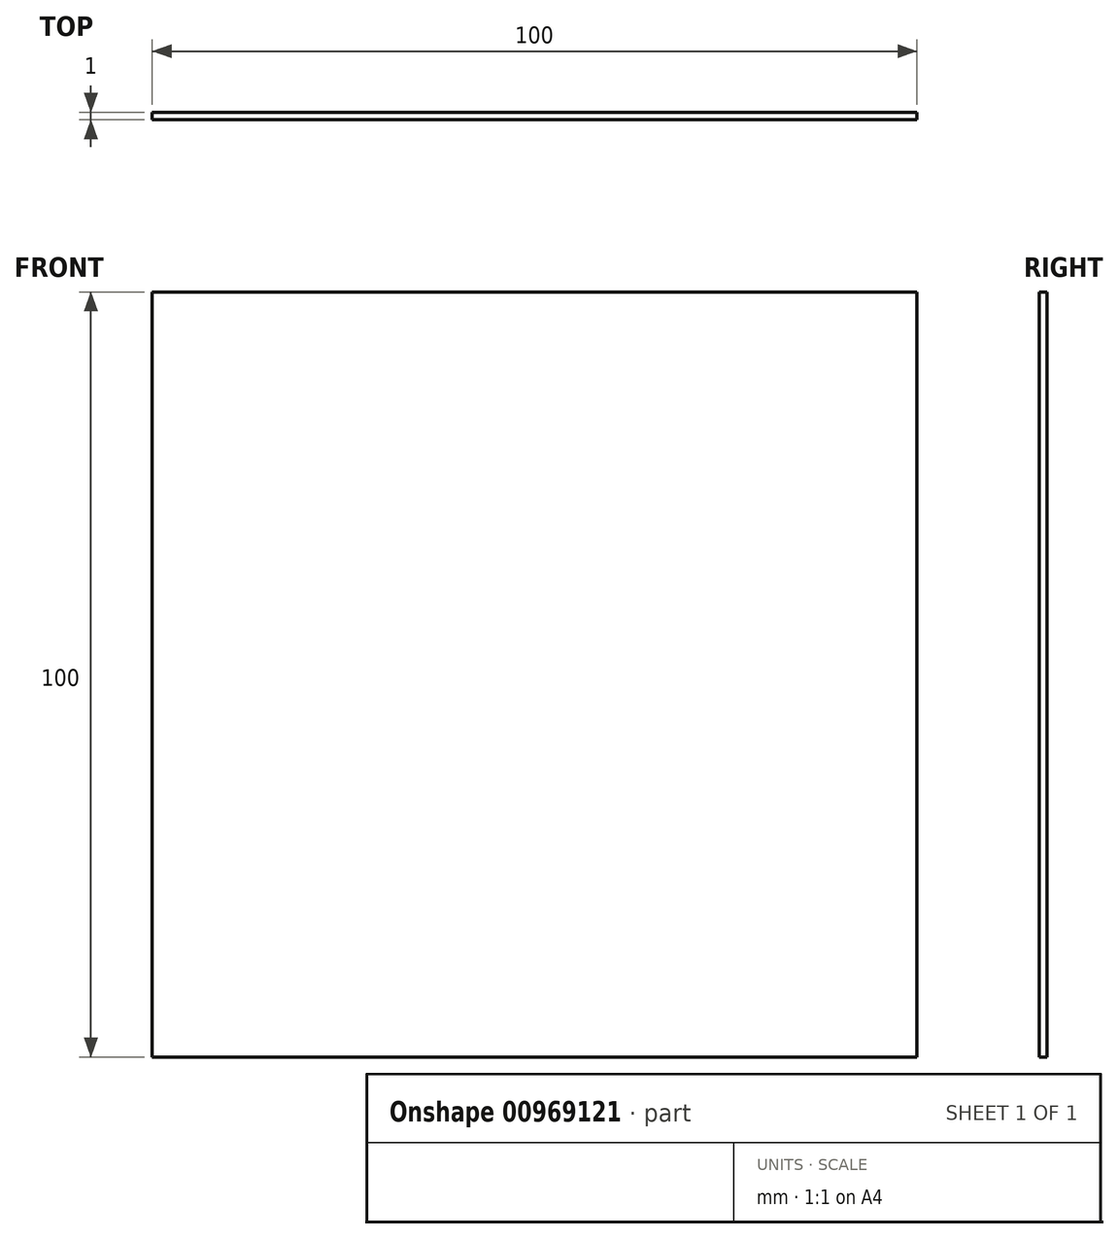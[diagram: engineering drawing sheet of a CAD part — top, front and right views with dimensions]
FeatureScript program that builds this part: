
annotation { "Feature Type Name" : "Feature", "Feature Type Description" : "" }
export const myFeature = defineFeature(function(context is Context, id is Id, definition is map)
    precondition{}
    {
        {
            var Q0;
            Q0=qCreatedBy(makeId("Front.planeOp"),FACE);
            var sketch = newSketch(context, id + "F0", { "sketchPlane" : qUnion([Q0])});
            skLineSegment(sketch, "E0.bottom", {"start": v(50, 50) * mm, "end": v(-50, 50) * mm});
            skLineSegment(sketch, "E0.top", {"start": v(50, -50) * mm, "end": v(-50, -50) * mm});
            skLineSegment(sketch, "E0.left", {"start": v(50, 50) * mm, "end": v(50, -50) * mm});
            skLineSegment(sketch, "E0.right", {"start": v(-50, 50) * mm, "end": v(-50, -50) * mm});
            skPoint(sketch, "E0.middle", {"position": v(0, 0) * mm});
            skSolve(sketch);
        }
        {
            var Q0;
            Q0=makeQuery(id+"F0.imprint","IMPRINT",FACE,{"disambiguationData":[TD([[makeQuery(id+"F0.imprint","IMPRINT",EDGE,{"derivedFrom":sQuery(id+"F0.wireOp",EDGE,"E0.bottom")}),1.0]])]});
            extrude(context, id + "F1", {"entities" : qUnion([Q0]), "depth" : 1 * mm, "offsetDistance" : 25 * mm});
        }
    });
